# Revit family: rba-bim-rba1631-100 and rba-bim-rba1631-300
name_source: partatom
category: Plumbing Fixtures
revit_build: Autodesk Revit 2018 (Build: 20170223_1515(x64)
units: mm (PartAtom-declared; Revit-internal decimal feet)

## family parameters
Always vertical = No
Cut with Voids When Loaded = No
Part Type = Normal
Room Calculation Point = No
Round Connector Dimension = Use Diameter
Shared = Yes
Work Plane-Based = No

## types (2) — shared parameters
CW Connection = Yes
Description = ōken Robe Hook
HW Connection = Yes
Manufacturer = RBA Group
Vent Connection = Yes
Waste Connection = Yes

## per-type parameters (varying)
| type | Logo Black | Logo White | Materials and Finishes | Modified Issue |
| RBA1631-100 | Yes | No | Heavy Duty Brass in a Bright Chrome Finish | 20220519.01 |
| RBA1631-300 | No | Yes | Heavy Duty Brass in a Matte Black Finish | 20190924.01 |

note: column(s) folded — value = type name in every type: Model

## geometry (parser evidence)
native form markers: Blend x2, Sweep x3
no freeform markers — native parametric forms only
